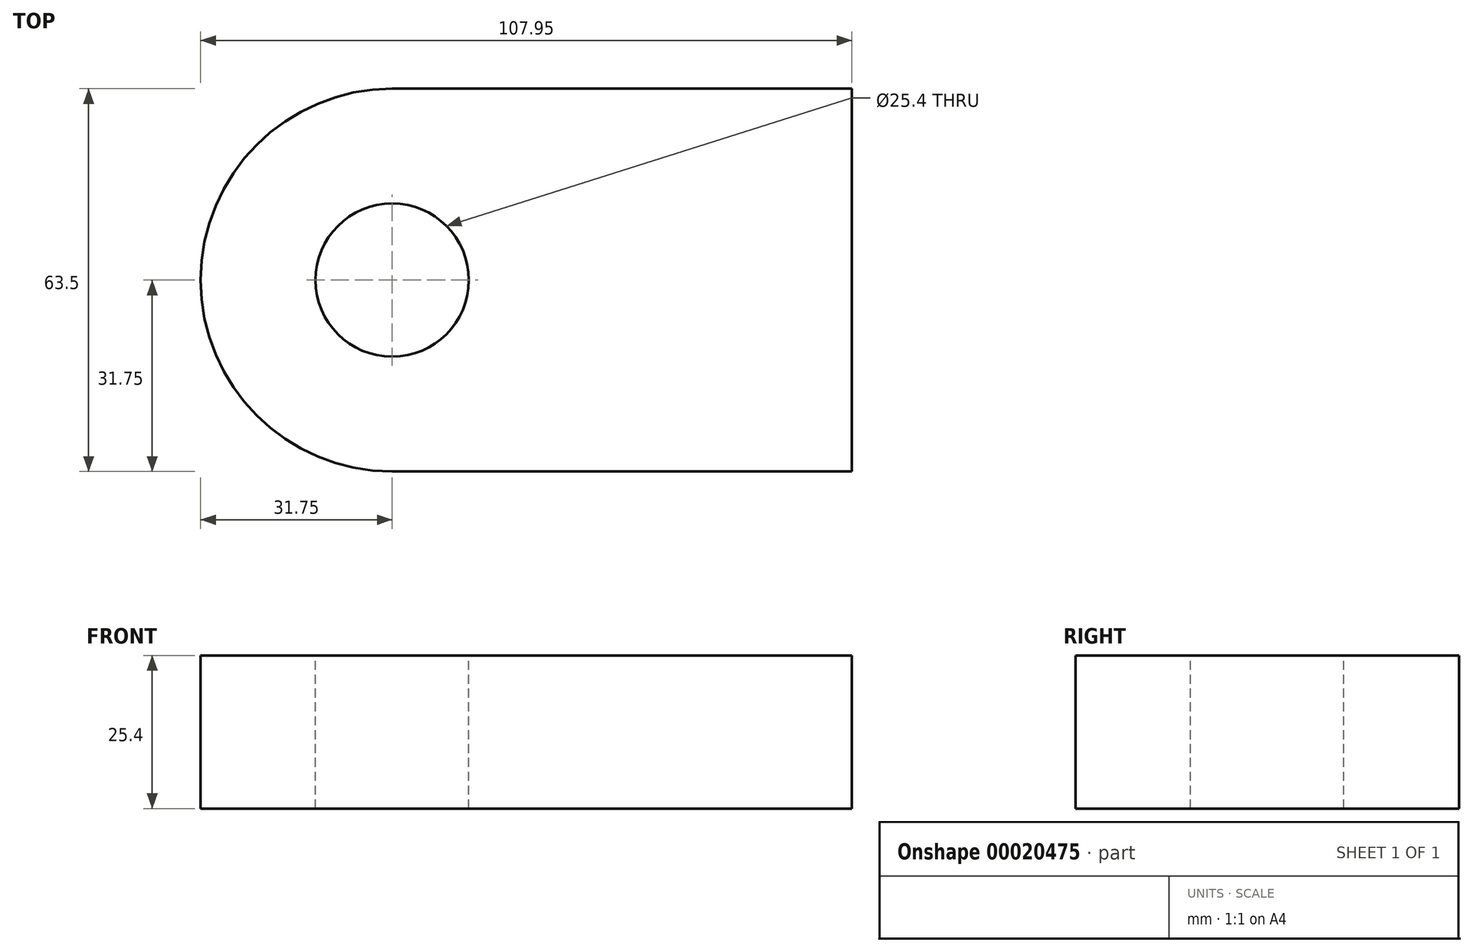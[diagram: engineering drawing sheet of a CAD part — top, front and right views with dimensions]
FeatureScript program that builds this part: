
annotation { "Feature Type Name" : "Feature", "Feature Type Description" : "" }
export const myFeature = defineFeature(function(context is Context, id is Id, definition is map)
    precondition{}
    {
        {
            var Q0;
            Q0=qCreatedBy(makeId("Top.planeOp"),FACE);
            var sketch = newSketch(context, id + "F0", { "sketchPlane" : qUnion([Q0])});
            skLineSegment(sketch, "E0.rect.bottom", {"start": v(-38.1, 31.75) * mm, "end": v(38.1, 31.75) * mm});
            skLineSegment(sketch, "E0.rect.top", {"start": v(-38.1, -31.75) * mm, "end": v(38.1, -31.75) * mm});
            skLineSegment(sketch, "E0.rect.left", {"start": v(-38.1, 31.75) * mm, "end": v(-38.1, -31.75) * mm});
            skLineSegment(sketch, "E0.rect.right", {"start": v(38.1, 31.75) * mm, "end": v(38.1, -31.75) * mm});
            skPoint(sketch, "E0.rect.middle", {"position": v(0, 0) * mm});
            skCircle(sketch, "E1", {"center": v(-38.1, 0) * mm, "radius": 31.75 * mm});
            skCircle(sketch, "E2", {"center": v(-38.1, 0) * mm, "radius": 12.7 * mm});
            skSolve(sketch);
        }
        {
            var Q0;
            {var subQ0=sQuery(id+"F0.wireOp",EDGE,"E2");var subQ1=sQuery(id+"F0.wireOp",EDGE,"E0.rect.left");var subQ3=makeQuery(id+"F0.imprint","INTERSECT",VERTEX,{"disambiguationData":[OD(0.0)],"derivedFrom":[subQ1,subQ0]});Q0=makeQuery(id+"F0.imprint","IMPRINT",FACE,{"disambiguationData":[TD([[makeQuery(id+"F0.imprint","IMPRINT",EDGE,{"disambiguationData":[TD([[subQ3,-1.0]])],"derivedFrom":subQ0}),-1.0]])]});}
            var Q1;
            {var subQ0=sQuery(id+"F0.wireOp",EDGE,"E2");var subQ1=sQuery(id+"F0.wireOp",EDGE,"E0.rect.left");var subQ3=makeQuery(id+"F0.imprint","INTERSECT",VERTEX,{"disambiguationData":[OD(0.0)],"derivedFrom":[subQ1,subQ0]});Q1=makeQuery(id+"F0.imprint","IMPRINT",FACE,{"disambiguationData":[TD([[makeQuery(id+"F0.imprint","IMPRINT",EDGE,{"disambiguationData":[TD([[subQ3,1.0]])],"derivedFrom":subQ0}),-1.0]])]});}
            var Q2;
            {var subQ3=sQuery(id+"F0.wireOp",EDGE,"E0.rect.bottom");Q2=makeQuery(id+"F0.imprint","IMPRINT",FACE,{"disambiguationData":[TD([[makeQuery(id+"F0.imprint","IMPRINT",EDGE,{"derivedFrom":subQ3}),-1.0]])]});}
            extrude(context, id + "F1", {"entities" : qUnion([Q0, Q1, Q2]), "oppositeDirection" : true, "depth" : 25.4 * mm});
        }
    });
